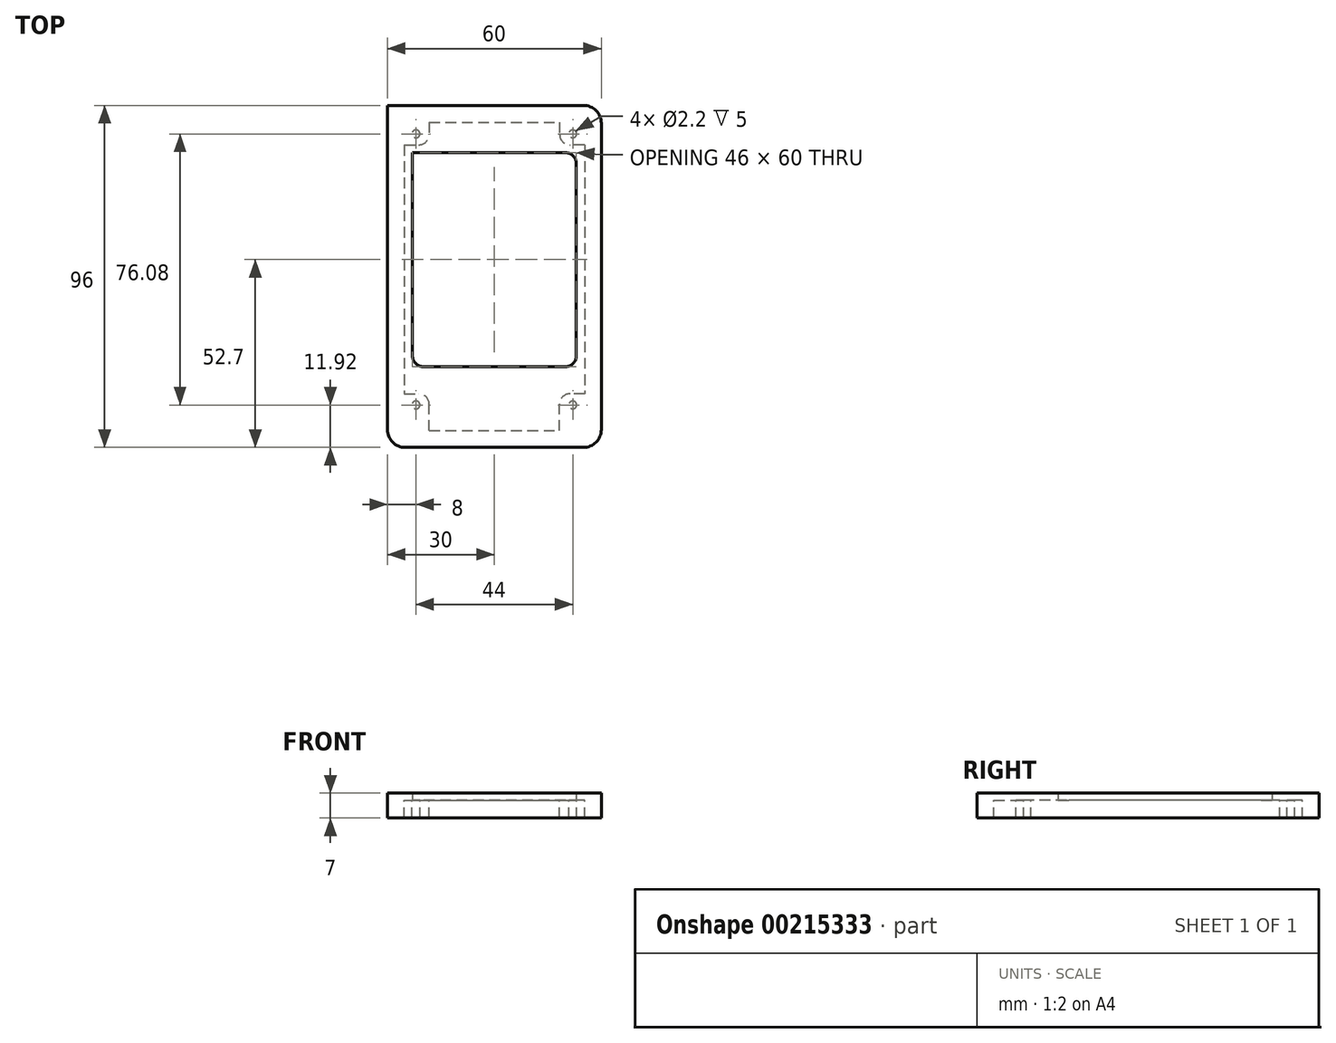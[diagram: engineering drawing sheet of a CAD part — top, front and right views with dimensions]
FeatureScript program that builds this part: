
annotation { "Feature Type Name" : "Feature", "Feature Type Description" : "" }
export const myFeature = defineFeature(function(context is Context, id is Id, definition is map)
    precondition{}
    {
        {
            var Q0;
            Q0=qCreatedBy(makeId("Top.planeOp"),FACE);
            var sketch = newSketch(context, id + "F0", { "sketchPlane" : qUnion([Q0])});
            skPoint(sketch, "E0.middle", {"position": v(0, 0) * mm});
            skCircle(sketch, "E1", {"center": v(-22, 40) * mm, "radius": 1.5 * mm});
            skCircle(sketch, "E2", {"center": v(22, 40) * mm, "radius": 1.5 * mm});
            skCircle(sketch, "E3", {"center": v(-22, -36.08) * mm, "radius": 1.5 * mm});
            skCircle(sketch, "E4", {"center": v(22, -36.08) * mm, "radius": 1.5 * mm});
            skLineSegment(sketch, "E5.bottom", {"start": v(25, -48) * mm, "end": v(-25, -48) * mm});
            skLineSegment(sketch, "E5.top", {"start": v(25, 48) * mm, "end": v(-27, 48) * mm});
            skLineSegment(sketch, "E5.left", {"start": v(30, -43) * mm, "end": v(30, 43) * mm});
            skLineSegment(sketch, "E5.right", {"start": v(-30, -43) * mm, "end": v(-30, 43) * mm});
            skPoint(sketch, "E6.visualSharp", {"position": v(-30, 48) * mm});
            skPoint(sketch, "E7.visualSharp", {"position": v(30, 48) * mm});
            skLineSegment(sketch, "E8.top", {"start": v(-30, 48) * mm, "end": v(-27, 48) * mm});
            skLineSegment(sketch, "E8.left", {"start": v(-30, 43) * mm, "end": v(-30, 48) * mm});
            skArc(sketch, "E9.filletArc", {"start": v(30, 43) * mm, "mid": v(28.54, 46.54) * mm, "end": v(25, 48) * mm});
            skPoint(sketch, "E10.visualSharp", {"position": v(30, -48) * mm});
            skArc(sketch, "E10.filletArc", {"start": v(25, -48) * mm, "mid": v(28.54, -46.54) * mm, "end": v(30, -43) * mm});
            skPoint(sketch, "E11.visualSharp", {"position": v(-30, -48) * mm});
            skArc(sketch, "E11.filletArc", {"start": v(-30, -43) * mm, "mid": v(-28.54, -46.54) * mm, "end": v(-25, -48) * mm});
            skSolve(sketch);
        }
        {
            var Q0;
            Q0=qSketchRegion(id+"F0",true);
            extrude(context, id + "F1", {"entities" : qUnion([Q0]), "depth" : 5 * mm});
        }
        {
            var Q0;
            Q0=makeQuery(id+"F1.opExtrude","CAP_FACE",FACE,{"disambiguationData":[OSD([sQuery(id+"F0.wireOp",EDGE,"E1"),sQuery(id+"F0.wireOp",EDGE,"E2"),sQuery(id+"F0.wireOp",EDGE,"E3"),sQuery(id+"F0.wireOp",EDGE,"E4"),sQuery(id+"F0.wireOp",EDGE,"E5.bottom"),sQuery(id+"F0.wireOp",EDGE,"E5.top"),sQuery(id+"F0.wireOp",EDGE,"E5.left"),sQuery(id+"F0.wireOp",EDGE,"E5.right")])],"isStart":false});
            var sketch = newSketch(context, id + "F2", { "sketchPlane" : qUnion([Q0])});
            skLineSegment(sketch, "E12.bottom", {"start": v(-25.3, 43.3) * mm, "end": v(25.3, 43.3) * mm});
            skLineSegment(sketch, "E12.top", {"start": v(-25.3, -43.3) * mm, "end": v(25.3, -43.3) * mm});
            skLineSegment(sketch, "E12.left", {"start": v(-25.3, 43.3) * mm, "end": v(-25.3, -43.3) * mm});
            skLineSegment(sketch, "E12.right", {"start": v(25.3, 43.3) * mm, "end": v(25.3, -43.3) * mm});
            skPoint(sketch, "E12.middle", {"position": v(0, 0) * mm});
            skCircle(sketch, "E13", {"center": v(-22, 40) * mm, "radius": 1.5 * mm});
            skCircle(sketch, "E14", {"center": v(22, 40) * mm, "radius": 1.5 * mm});
            skCircle(sketch, "E15", {"center": v(-22, -36.08) * mm, "radius": 1.5 * mm});
            skCircle(sketch, "E16", {"center": v(22, -36.08) * mm, "radius": 1.5 * mm});
            skSolve(sketch);
        }
        {
            var Q0;
            Q0=qSketchRegion(id+"F2",true);
            extrude(context, id + "F3", {"entities" : qUnion([Q0]), "operationType" : NewBodyOperationType.REMOVE, "oppositeDirection" : true, "depth" : 5 * mm});
        }
        {
            var Q0;
            Q0=makeQuery(id+"F1.opExtrude","CAP_FACE",FACE,{"disambiguationData":[OSD([sQuery(id+"F0.wireOp",EDGE,"E1"),sQuery(id+"F0.wireOp",EDGE,"E2"),sQuery(id+"F0.wireOp",EDGE,"E3"),sQuery(id+"F0.wireOp",EDGE,"E4"),sQuery(id+"F0.wireOp",EDGE,"E5.bottom"),sQuery(id+"F0.wireOp",EDGE,"E5.top"),sQuery(id+"F0.wireOp",EDGE,"E5.left"),sQuery(id+"F0.wireOp",EDGE,"E5.right")])],"isStart":false});
            var sketch = newSketch(context, id + "F4", { "sketchPlane" : qUnion([Q0])});
            skCircle(sketch, "E17", {"center": v(-22, 40) * mm, "radius": 1.1 * mm});
            skCircle(sketch, "E18", {"center": v(22, 40) * mm, "radius": 1.1 * mm});
            skCircle(sketch, "E19", {"center": v(22, -36.08) * mm, "radius": 1.1 * mm});
            skCircle(sketch, "E20", {"center": v(-22, -36.08) * mm, "radius": 1.1 * mm});
            skLineSegment(sketch, "E21.bottom", {"start": v(-25.3, 43.3) * mm, "end": v(-18.3, 43.3) * mm});
            skLineSegment(sketch, "E21.top", {"start": v(-25.3, 36.9) * mm, "end": v(-21.3, 36.9) * mm});
            skLineSegment(sketch, "E21.left", {"start": v(-25.3, 43.3) * mm, "end": v(-25.3, 36.9) * mm});
            skLineSegment(sketch, "E21.right", {"start": v(-18.3, 43.3) * mm, "end": v(-18.3, 39.9) * mm});
            skPoint(sketch, "E22.visualSharp", {"position": v(-18.3, 36.9) * mm});
            skArc(sketch, "E22.filletArc", {"start": v(-21.3, 36.9) * mm, "mid": v(-19.18, 37.78) * mm, "end": v(-18.3, 39.9) * mm});
            skLineSegment(sketch, "E23.bottom", {"start": v(25.3, 43.3) * mm, "end": v(18.3, 43.3) * mm});
            skLineSegment(sketch, "E23.top", {"start": v(25.3, 36.9) * mm, "end": v(21.3, 36.9) * mm});
            skLineSegment(sketch, "E23.left", {"start": v(25.3, 43.3) * mm, "end": v(25.3, 36.9) * mm});
            skLineSegment(sketch, "E23.right", {"start": v(18.3, 43.3) * mm, "end": v(18.3, 39.9) * mm});
            skPoint(sketch, "E24.visualSharp", {"position": v(18.3, 36.9) * mm});
            skArc(sketch, "E24.filletArc", {"start": v(18.3, 39.9) * mm, "mid": v(19.18, 37.78) * mm, "end": v(21.3, 36.9) * mm});
            skLineSegment(sketch, "E25.bottom", {"start": v(25.3, -43.3) * mm, "end": v(18.3, -43.3) * mm});
            skLineSegment(sketch, "E25.top", {"start": v(25.3, -32.9) * mm, "end": v(21.3, -32.9) * mm});
            skLineSegment(sketch, "E25.left", {"start": v(25.3, -43.3) * mm, "end": v(25.3, -32.9) * mm});
            skLineSegment(sketch, "E25.right", {"start": v(18.3, -43.3) * mm, "end": v(18.3, -35.9) * mm});
            skPoint(sketch, "E26.visualSharp", {"position": v(18.3, -32.9) * mm});
            skArc(sketch, "E26.filletArc", {"start": v(21.3, -32.9) * mm, "mid": v(19.18, -33.78) * mm, "end": v(18.3, -35.9) * mm});
            skLineSegment(sketch, "E27.bottom", {"start": v(-25.3, -43.3) * mm, "end": v(-18.3, -43.3) * mm});
            skLineSegment(sketch, "E27.top", {"start": v(-25.3, -32.9) * mm, "end": v(-21.3, -32.9) * mm});
            skLineSegment(sketch, "E27.left", {"start": v(-25.3, -43.3) * mm, "end": v(-25.3, -32.9) * mm});
            skLineSegment(sketch, "E27.right", {"start": v(-18.3, -43.3) * mm, "end": v(-18.3, -35.9) * mm});
            skPoint(sketch, "E28.visualSharp", {"position": v(-18.3, -32.9) * mm});
            skArc(sketch, "E28.filletArc", {"start": v(-18.3, -35.9) * mm, "mid": v(-19.18, -33.78) * mm, "end": v(-21.3, -32.9) * mm});
            skPoint(sketch, "E29.middle", {"position": v(0, 2) * mm});
            skPoint(sketch, "E29.left.start.orphan", {"position": v(-25, 36.6) * mm});
            skPoint(sketch, "E29.right.start.orphan", {"position": v(25, 36.6) * mm});
            skPoint(sketch, "E29.top.end.orphan", {"position": v(25, -32.6) * mm});
            skPoint(sketch, "E29.top.start.orphan", {"position": v(-25, -32.6) * mm});
            skSolve(sketch);
        }
        {
            var Q0;
            Q0=qSketchRegion(id+"F4",true);
            extrude(context, id + "F5", {"entities" : qUnion([Q0]), "operationType" : NewBodyOperationType.ADD, "oppositeDirection" : true, "depth" : 5 * mm});
        }
        {
            var Q0;
            Q0=makeQuery(id+"F5.boolean.opBoolean","MERGE",FACE,{"derivedFrom":[makeQuery(id+"F1.opExtrude","CAP_FACE",FACE,{"disambiguationData":[OSD([sQuery(id+"F0.wireOp",EDGE,"E1"),sQuery(id+"F0.wireOp",EDGE,"E2"),sQuery(id+"F0.wireOp",EDGE,"E3"),sQuery(id+"F0.wireOp",EDGE,"E4"),sQuery(id+"F0.wireOp",EDGE,"E5.bottom"),sQuery(id+"F0.wireOp",EDGE,"E5.top"),sQuery(id+"F0.wireOp",EDGE,"E5.left"),sQuery(id+"F0.wireOp",EDGE,"E5.right"),sQuery(id+"F0.wireOp",EDGE,"E8.top"),sQuery(id+"F0.wireOp",EDGE,"E8.left"),sQuery(id+"F0.wireOp",EDGE,"E9.filletArc"),sQuery(id+"F0.wireOp",EDGE,"E10.filletArc"),sQuery(id+"F0.wireOp",EDGE,"E11.filletArc")])],"isStart":false}),makeQuery(id+"F5.opExtrude","CAP_FACE",FACE,{"disambiguationData":[OSD([sQuery(id+"F4.wireOp",EDGE,"E17"),sQuery(id+"F4.wireOp",EDGE,"E21.bottom"),sQuery(id+"F4.wireOp",EDGE,"E21.top"),sQuery(id+"F4.wireOp",EDGE,"E21.left"),sQuery(id+"F4.wireOp",EDGE,"E21.right"),sQuery(id+"F4.wireOp",EDGE,"E22.filletArc")])],"isStart":true}),makeQuery(id+"F5.opExtrude","CAP_FACE",FACE,{"disambiguationData":[OSD([sQuery(id+"F4.wireOp",EDGE,"E18"),sQuery(id+"F4.wireOp",EDGE,"E23.bottom"),sQuery(id+"F4.wireOp",EDGE,"E23.top"),sQuery(id+"F4.wireOp",EDGE,"E23.left"),sQuery(id+"F4.wireOp",EDGE,"E23.right"),sQuery(id+"F4.wireOp",EDGE,"E24.filletArc")])],"isStart":true}),makeQuery(id+"F5.opExtrude","CAP_FACE",FACE,{"disambiguationData":[OSD([sQuery(id+"F4.wireOp",EDGE,"E19"),sQuery(id+"F4.wireOp",EDGE,"E25.bottom"),sQuery(id+"F4.wireOp",EDGE,"E25.top"),sQuery(id+"F4.wireOp",EDGE,"E25.left"),sQuery(id+"F4.wireOp",EDGE,"E25.right"),sQuery(id+"F4.wireOp",EDGE,"E26.filletArc")])],"isStart":true}),makeQuery(id+"F5.opExtrude","CAP_FACE",FACE,{"disambiguationData":[OSD([sQuery(id+"F4.wireOp",EDGE,"E20"),sQuery(id+"F4.wireOp",EDGE,"E27.bottom"),sQuery(id+"F4.wireOp",EDGE,"E27.top"),sQuery(id+"F4.wireOp",EDGE,"E27.left"),sQuery(id+"F4.wireOp",EDGE,"E27.right"),sQuery(id+"F4.wireOp",EDGE,"E28.filletArc")])],"isStart":true})]});
            var sketch = newSketch(context, id + "F6", { "sketchPlane" : qUnion([Q0])});
            skLineSegment(sketch, "E30.bottom", {"start": v(-20, 34.7) * mm, "end": v(20, 34.7) * mm});
            skLineSegment(sketch, "E30.top", {"start": v(-20, -25.3) * mm, "end": v(20, -25.3) * mm});
            skLineSegment(sketch, "E30.left", {"start": v(-23, 31.7) * mm, "end": v(-23, -22.3) * mm});
            skLineSegment(sketch, "E30.right", {"start": v(23, 31.7) * mm, "end": v(23, -22.3) * mm});
            skPoint(sketch, "E30.middle", {"position": v(0, 4.7) * mm});
            skPoint(sketch, "E31.visualSharp", {"position": v(23, 34.7) * mm});
            skArc(sketch, "E31.filletArc", {"start": v(23, 31.7) * mm, "mid": v(22.12, 33.82) * mm, "end": v(20, 34.7) * mm});
            skPoint(sketch, "E32.visualSharp", {"position": v(-23, 34.7) * mm});
            skPoint(sketch, "E33.visualSharp", {"position": v(-23, -25.3) * mm});
            skArc(sketch, "E33.filletArc", {"start": v(-23, -22.3) * mm, "mid": v(-22.12, -24.42) * mm, "end": v(-20, -25.3) * mm});
            skPoint(sketch, "E34.visualSharp", {"position": v(23, -25.3) * mm});
            skArc(sketch, "E34.filletArc", {"start": v(20, -25.3) * mm, "mid": v(22.12, -24.42) * mm, "end": v(23, -22.3) * mm});
            skLineSegment(sketch, "E35.bottom", {"start": v(-30, 48) * mm, "end": v(25, 48) * mm});
            skLineSegment(sketch, "E35.top", {"start": v(-25, -48) * mm, "end": v(25, -48) * mm});
            skLineSegment(sketch, "E35.left", {"start": v(-30, 48) * mm, "end": v(-30, -43) * mm});
            skLineSegment(sketch, "E35.right", {"start": v(30, 43) * mm, "end": v(30, -43) * mm});
            skPoint(sketch, "E35.middle", {"position": v(0, 0) * mm});
            skPoint(sketch, "E36.visualSharp", {"position": v(30, 48) * mm});
            skArc(sketch, "E36.filletArc", {"start": v(30, 43) * mm, "mid": v(28.54, 46.54) * mm, "end": v(25, 48) * mm});
            skPoint(sketch, "E37.visualSharp", {"position": v(30, -48) * mm});
            skArc(sketch, "E37.filletArc", {"start": v(25, -48) * mm, "mid": v(28.54, -46.54) * mm, "end": v(30, -43) * mm});
            skPoint(sketch, "E38.visualSharp", {"position": v(-30, -48) * mm});
            skArc(sketch, "E38.filletArc", {"start": v(-30, -43) * mm, "mid": v(-28.54, -46.54) * mm, "end": v(-25, -48) * mm});
            skLineSegment(sketch, "E39", {"start": v(-23, 31.7) * mm, "end": v(-23, 34.7) * mm});
            skLineSegment(sketch, "E40", {"start": v(-20, 34.7) * mm, "end": v(-23, 34.7) * mm});
            skSolve(sketch);
        }
        {
            var Q0;
            Q0 = qSketchRegion(id + "F6", true);
            extrude(context, id + "F7", {"entities" : qUnion([Q0]), "operationType" : NewBodyOperationType.ADD, "depth" : 2 * mm});
        }
    });
